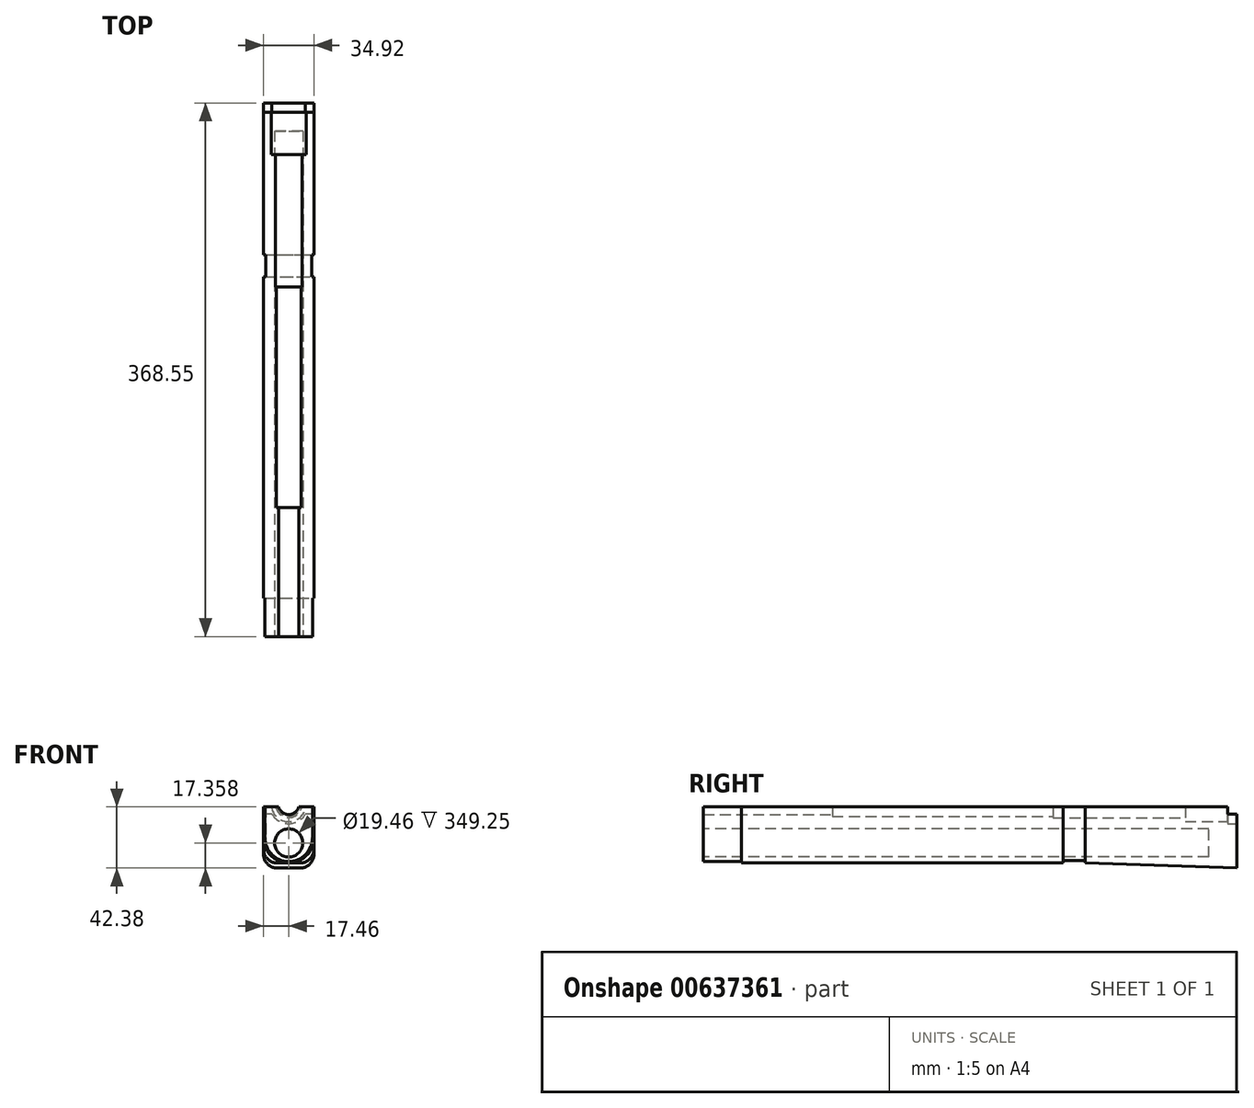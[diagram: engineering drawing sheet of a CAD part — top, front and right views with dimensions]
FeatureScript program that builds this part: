
annotation { "Feature Type Name" : "Feature", "Feature Type Description" : "" }
export const myFeature = defineFeature(function(context is Context, id is Id, definition is map)
    precondition{}
    {
        {
            var Q0;
            Q0=qCreatedBy(makeId("Front.planeOp"),FACE);
            var sketch = newSketch(context, id + "F0", { "sketchPlane" : qUnion([Q0])});
            skLineSegment(sketch, "E0", {"start": v(-17.45, -47.24) * mm, "end": v(17.45, -47.24) * mm});
            skLineSegment(sketch, "E1", {"start": v(-16.13, -1.78) * mm, "end": v(-16.13, -47.24) * mm});
            skLineSegment(sketch, "E2", {"start": v(16.13, -47.24) * mm, "end": v(16.13, -1.78) * mm});
            skLineSegment(sketch, "E3", {"start": v(-17.45, -1.78) * mm, "end": v(-17.45, -47.24) * mm});
            skLineSegment(sketch, "E4", {"start": v(17.45, -1.78) * mm, "end": v(12.57, -1.78) * mm});
            skLineSegment(sketch, "E5.trimOffspring", {"start": v(-12.57, -1.78) * mm, "end": v(-17.45, -1.78) * mm});
            skArc(sketch, "E6.converted", {"start": v(-12.57, -1.78) * mm, "mid": v(0, -12.7) * mm, "end": v(12.57, -1.78) * mm});
            skLineSegment(sketch, "E7", {"start": v(17.45, -6.83) * mm, "end": v(11.6, -6.83) * mm});
            skLineSegment(sketch, "E8", {"start": v(17.45, -1.78) * mm, "end": v(17.45, -47.24) * mm});
            skLineSegment(sketch, "E9.trimOffspring", {"start": v(-11.6, -6.83) * mm, "end": v(-17.45, -6.83) * mm});
            skArc(sketch, "E10.0", {"start": v(-13.34, -1.78) * mm, "mid": v(0, -13.46) * mm, "end": v(13.34, -1.78) * mm});
            skSolve(sketch);
        }
        {
            var Q0;
            {var subQ2=sQuery(id+"F0.wireOp",EDGE,"E2");Q0=makeQuery(id+"F0.imprint","IMPRINT",FACE,{"disambiguationData":[TD([[makeQuery(id+"F0.imprint","IMPRINT",EDGE,{"derivedFrom":subQ2}),-1.0]])]});}
            var Q1;
            {var subQ2=sQuery(id+"F0.wireOp",EDGE,"E1");Q1=makeQuery(id+"F0.imprint","IMPRINT",FACE,{"disambiguationData":[TD([[makeQuery(id+"F0.imprint","IMPRINT",EDGE,{"derivedFrom":subQ2}),-1.0]])]});}
            var Q2;
            {var subQ4=sQuery(id+"F0.wireOp",EDGE,"E1");Q2=makeQuery(id+"F0.imprint","IMPRINT",FACE,{"disambiguationData":[TD([[makeQuery(id+"F0.imprint","IMPRINT",EDGE,{"derivedFrom":subQ4}),1.0]])]});}
            var Q3;
            {var subQ0=sQuery(id+"F0.wireOp",EDGE,"E4");var subQ1=sQuery(id+"F0.wireOp",EDGE,"E2");var subQ2=makeQuery(id+"F0.imprint","INTERSECT",VERTEX,{"derivedFrom":[subQ1,subQ0]});Q3=makeQuery(id+"F0.imprint","IMPRINT",FACE,{"disambiguationData":[TD([[makeQuery(id+"F0.imprint","IMPRINT",EDGE,{"disambiguationData":[TD([[subQ2,1.0]])],"derivedFrom":subQ1}),1.0]])]});}
            var Q4;
            {var subQ0=sQuery(id+"F0.wireOp",EDGE,"E4");var subQ1=sQuery(id+"F0.wireOp",EDGE,"E2");var subQ2=makeQuery(id+"F0.imprint","INTERSECT",VERTEX,{"derivedFrom":[subQ1,subQ0]});Q4=makeQuery(id+"F0.imprint","IMPRINT",FACE,{"disambiguationData":[TD([[makeQuery(id+"F0.imprint","IMPRINT",EDGE,{"disambiguationData":[TD([[subQ2,1.0]])],"derivedFrom":subQ1}),-1.0]])]});}
            var Q5;
            {var subQ0=sQuery(id+"F0.wireOp",EDGE,"E5.trimOffspring");var subQ1=sQuery(id+"F0.wireOp",EDGE,"E1");var subQ2=makeQuery(id+"F0.imprint","INTERSECT",VERTEX,{"derivedFrom":[subQ1,subQ0]});Q5=makeQuery(id+"F0.imprint","IMPRINT",FACE,{"disambiguationData":[TD([[makeQuery(id+"F0.imprint","IMPRINT",EDGE,{"disambiguationData":[TD([[subQ2,-1.0]])],"derivedFrom":subQ1}),-1.0]])]});}
            var Q6;
            {var subQ5=sQuery(id+"F0.wireOp",EDGE,"E0");var subQ7=sQuery(id+"F0.wireOp",EDGE,"E1");var subQ8=makeQuery(id+"F0.imprint","INTERSECT",VERTEX,{"derivedFrom":[subQ5,subQ7]});Q6=makeQuery(id+"F0.imprint","IMPRINT",FACE,{"disambiguationData":[TD([[makeQuery(id+"F0.imprint","IMPRINT",EDGE,{"disambiguationData":[TD([[subQ8,-1.0]])],"derivedFrom":subQ5}),1.0]])]});}
            extrude(context, id + "F1", {"entities" : qUnion([Q0, Q1, Q2, Q3, Q4, Q5, Q6]), "depth" : 6.35 * mm, "offsetDistance" : 25.4 * mm});
        }
        {
            var Q0;
            Q0=makeQuery(id+"F1.opExtrude","CAP_FACE",FACE,{"disambiguationData":[OSD([sQuery(id+"F0.wireOp",EDGE,"E0"),sQuery(id+"F0.wireOp",EDGE,"8edb2757-4879-4a96-b7e5-693a79a6b6a4"),sQuery(id+"F0.wireOp",EDGE,"b94c221b-9bd1-4d43-af97-e907ac8222b8"),sQuery(id+"F0.wireOp",EDGE,"b538d115-4aab-44f9-98d3-6b26c575ee44"),sQuery(id+"F0.wireOp",EDGE,"78d40427-cc9b-45da-965b-9590cd821f86"),sQuery(id+"F0.wireOp",EDGE,"c01ce0f5-0f3a-4153-bfe7-1fc23657275d")])],"isStart":false});
            var sketch = newSketch(context, id + "F2", { "sketchPlane" : qUnion([Q0])});
            skLineSegment(sketch, "E11", {"start": v(-17.45, -47.24) * mm, "end": v(-17.45, -47.24) * mm});
            skArc(sketch, "E12", {"start": v(-11.93, -1.78) * mm, "mid": v(0, -12.07) * mm, "end": v(11.93, -1.78) * mm});
            skLineSegment(sketch, "E13", {"start": v(-16.13, -1.78) * mm, "end": v(-16.13, -47.24) * mm});
            skLineSegment(sketch, "E14", {"start": v(16.13, -1.78) * mm, "end": v(16.13, -47.24) * mm});
            skLineSegment(sketch, "E15", {"start": v(11.93, -1.78) * mm, "end": v(17.45, -1.78) * mm});
            skLineSegment(sketch, "E16", {"start": v(-11.93, -1.78) * mm, "end": v(-17.45, -1.78) * mm});
            skLineSegment(sketch, "E17", {"start": v(-17.45, -1.78) * mm, "end": v(-17.45, -47.24) * mm});
            skSolve(sketch);
        }
        {
            var Q0;
            {var subQ2=sQuery(id+"F2.wireOp",EDGE,"E13");Q0=makeQuery(id+"F2.imprint","IMPRINT",FACE,{"disambiguationData":[TD([[makeQuery(id+"F2.imprint","IMPRINT",EDGE,{"derivedFrom":subQ2}),1.0]])]});}
            var Q1;
            {var subQ0=sQuery(id+"F2.wireOp",EDGE,"E12");Q1=makeQuery(id+"F2.imprint","IMPRINT",FACE,{"disambiguationData":[TD([[makeQuery(id+"F2.imprint","IMPRINT",EDGE,{"derivedFrom":subQ0}),-1.0]])]});}
            var Q2;
            {var subQ0=sQuery(id+"F2.wireOp",EDGE,"E13");Q2=makeQuery(id+"F2.imprint","IMPRINT",FACE,{"disambiguationData":[TD([[makeQuery(id+"F2.imprint","IMPRINT",EDGE,{"derivedFrom":subQ0}),-1.0]])]});}
            var Q3;
            {var subQ0=sQuery(id+"F2.wireOp",EDGE,"E14");Q3=makeQuery(id+"F2.imprint","IMPRINT",FACE,{"disambiguationData":[TD([[makeQuery(id+"F2.imprint","IMPRINT",EDGE,{"derivedFrom":subQ0}),1.0]])]});}
            extrude(context, id + "F3", {"entities" : qUnion([Q0, Q1, Q2, Q3]), "operationType" : NewBodyOperationType.ADD, "depth" : 29.2 * mm, "offsetDistance" : 25.4 * mm});
        }
        {
            var Q0;
            Q0=makeQuery(id+"F3.opExtrude","CAP_FACE",FACE,{"disambiguationData":[OSD([sQuery(id+"F2.wireOp",EDGE,"E12"),sQuery(id+"F2.wireOp",EDGE,"E13"),sQuery(id+"F2.wireOp",EDGE,"E14"),sQuery(id+"F2.wireOp",EDGE,"f77e2a34-3a45-4c61-b7b2-087de49498f3"),sQuery(id+"F2.wireOp",EDGE,"be3fd59c-918e-4d32-9c2f-12a798890d1d"),sQuery(id+"F2.wireOp",EDGE,"E11")])],"isStart":false});
            var sketch = newSketch(context, id + "F4", { "sketchPlane" : qUnion([Q0])});
            skArc(sketch, "E18", {"start": v(-9.12, -1.78) * mm, "mid": v(0, -9.3) * mm, "end": v(9.12, -1.78) * mm});
            skLineSegment(sketch, "E19", {"start": v(-16.13, -1.78) * mm, "end": v(-16.13, -47.24) * mm});
            skLineSegment(sketch, "E20", {"start": v(16.13, -1.78) * mm, "end": v(16.13, -47.24) * mm});
            skLineSegment(sketch, "E21", {"start": v(17.45, -1.78) * mm, "end": v(9.12, -1.78) * mm});
            skLineSegment(sketch, "E22", {"start": v(-17.45, -1.78) * mm, "end": v(-9.12, -1.78) * mm});
            skLineSegment(sketch, "E23", {"start": v(-17.45, -47.24) * mm, "end": v(17.45, -47.24) * mm});
            skLineSegment(sketch, "E24", {"start": v(17.45, -47.24) * mm, "end": v(17.45, -1.78) * mm});
            skLineSegment(sketch, "E25", {"start": v(-17.45, -1.78) * mm, "end": v(-17.45, -47.24) * mm});
            skSolve(sketch);
        }
        {
            var Q0;
            Q0=qSketchRegion(id+"F4",true);
            extrude(context, id + "F5", {"entities" : qUnion([Q0]), "operationType" : NewBodyOperationType.ADD, "depth" : 69.06 * mm, "offsetDistance" : 25.4 * mm});
        }
        {
            var Q0;
            Q0=makeQuery(id+"F5.opExtrude","CAP_EDGE",EDGE,{"disambiguationData":[OSD([sQuery(id+"F4.wireOp",EDGE,"E23")])],"isStart":false});
            chamfer(context, id + "F6", {"entities" : qUnion([Q0]), "chamferType" : ChamferType.TWO_OFFSETS, "width1" : 6.6 * mm, "oppositeDirection" : false, "width2" : 196.06 * mm, "tangentPropagation" : true});
        }
        {
            var Q0;
            Q0=makeQuery(id+"F6.opChamfer","BLEND_EDGE",EDGE,{"blendedFrom":[makeQuery(id+"F5.opExtrude","CAP_EDGE",EDGE,{"disambiguationData":[OSD([sQuery(id+"F4.wireOp",EDGE,"E23")])],"isStart":false}),makeQuery(id+"F5.boolean.opBoolean","MERGE",FACE,{"derivedFrom":[makeQuery(id+"F3.boolean.opBoolean","MERGE",FACE,{"derivedFrom":[makeQuery(id+"F1.opExtrude","SWEPT_FACE",FACE,{"disambiguationData":[OSD([sQuery(id+"F0.wireOp",EDGE,"E3")])]}),makeQuery(id+"F3.opExtrude","SWEPT_FACE",FACE,{"disambiguationData":[OSD([sQuery(id+"F2.wireOp",EDGE,"E17")])]})]}),makeQuery(id+"F5.opExtrude","SWEPT_FACE",FACE,{"disambiguationData":[OSD([sQuery(id+"F4.wireOp",EDGE,"E25")])]})]})],"blendedInto":[makeQuery(id+"F5.boolean.opBoolean","MERGE",FACE,{"derivedFrom":[makeQuery(id+"F3.boolean.opBoolean","MERGE",FACE,{"derivedFrom":[makeQuery(id+"F1.opExtrude","SWEPT_FACE",FACE,{"disambiguationData":[OSD([sQuery(id+"F0.wireOp",EDGE,"E3")])]}),makeQuery(id+"F3.opExtrude","SWEPT_FACE",FACE,{"disambiguationData":[OSD([sQuery(id+"F2.wireOp",EDGE,"E17")])]})]}),makeQuery(id+"F5.opExtrude","SWEPT_FACE",FACE,{"disambiguationData":[OSD([sQuery(id+"F4.wireOp",EDGE,"E25")])]})]})]});
            var Q1;
            Q1=makeQuery(id+"F6.opChamfer","BLEND_EDGE",EDGE,{"blendedFrom":[makeQuery(id+"F5.opExtrude","CAP_EDGE",EDGE,{"disambiguationData":[OSD([sQuery(id+"F4.wireOp",EDGE,"E23")])],"isStart":false}),makeQuery(id+"F5.boolean.opBoolean","MERGE",FACE,{"derivedFrom":[makeQuery(id+"F3.boolean.opBoolean","MERGE",FACE,{"derivedFrom":[makeQuery(id+"F1.opExtrude","SWEPT_FACE",FACE,{"disambiguationData":[OSD([sQuery(id+"F0.wireOp",EDGE,"2a34f45b-83aa-449b-ac8a-cdb24f63008b")])]}),makeQuery(id+"F3.opExtrude","SWEPT_FACE",FACE,{"disambiguationData":[OSD([sQuery(id+"F2.wireOp",EDGE,"fa13c2eb-5be7-4b32-a947-3f863f632ee6")])]})]}),makeQuery(id+"F5.opExtrude","SWEPT_FACE",FACE,{"disambiguationData":[OSD([sQuery(id+"F4.wireOp",EDGE,"E24")])]})]})],"blendedInto":[makeQuery(id+"F5.boolean.opBoolean","MERGE",FACE,{"derivedFrom":[makeQuery(id+"F3.boolean.opBoolean","MERGE",FACE,{"derivedFrom":[makeQuery(id+"F1.opExtrude","SWEPT_FACE",FACE,{"disambiguationData":[OSD([sQuery(id+"F0.wireOp",EDGE,"2a34f45b-83aa-449b-ac8a-cdb24f63008b")])]}),makeQuery(id+"F3.opExtrude","SWEPT_FACE",FACE,{"disambiguationData":[OSD([sQuery(id+"F2.wireOp",EDGE,"fa13c2eb-5be7-4b32-a947-3f863f632ee6")])]})]}),makeQuery(id+"F5.opExtrude","SWEPT_FACE",FACE,{"disambiguationData":[OSD([sQuery(id+"F4.wireOp",EDGE,"E24")])]})]})]});
            fillet(context, id + "F7", {"entities" : qUnion([Q0, Q1]), "radius" : 9.65 * mm, "tangentPropagation" : true, "allowEdgeOverflow" : false});
        }
        {
            var Q0;
            Q0=makeQuery(id+"F5.opExtrude","CAP_FACE",FACE,{"disambiguationData":[OSD([sQuery(id+"F4.wireOp",EDGE,"E18"),sQuery(id+"F4.wireOp",EDGE,"E21"),sQuery(id+"F4.wireOp",EDGE,"E22"),sQuery(id+"F4.wireOp",EDGE,"E23"),sQuery(id+"F4.wireOp",EDGE,"E24"),sQuery(id+"F4.wireOp",EDGE,"E25")])],"isStart":false});
            var sketch = newSketch(context, id + "F8", { "sketchPlane" : qUnion([Q0])});
            skLineSegment(sketch, "E26.0", {"start": v(-15.92, -1.78) * mm, "end": v(-15.93, -23.19) * mm});
            skLineSegment(sketch, "E27.0", {"start": v(15.92, -1.78) * mm, "end": v(15.93, -23.19) * mm});
            skArc(sketch, "E28", {"start": v(-15.93, -23.19) * mm, "mid": v(0, -39.12) * mm, "end": v(15.93, -23.19) * mm});
            skLineSegment(sketch, "E29", {"start": v(-15.92, -1.78) * mm, "end": v(-9.12, -1.78) * mm});
            skLineSegment(sketch, "E30", {"start": v(15.92, -1.78) * mm, "end": v(9.12, -1.78) * mm});
            skArc(sketch, "E31", {"start": v(-9.12, -1.78) * mm, "mid": v(0, -9.3) * mm, "end": v(9.12, -1.78) * mm});
            skSolve(sketch);
        }
        {
            var Q0;
            Q0=makeQuery(id+"F8.imprint","IMPRINT",FACE,{"disambiguationData":[TD([[makeQuery(id+"F8.imprint","IMPRINT",EDGE,{"derivedFrom":sQuery(id+"F8.wireOp",EDGE,"E26.0")}),1.0]])]});
            extrude(context, id + "F9", {"entities" : qUnion([Q0]), "operationType" : NewBodyOperationType.ADD, "depth" : 15.42 * mm, "offsetDistance" : 25.4 * mm});
        }
        {
            var Q0;
            Q0=makeQuery(id+"F9.opExtrude","CAP_FACE",FACE,{"disambiguationData":[OSD([sQuery(id+"F8.wireOp",EDGE,"E26.0"),sQuery(id+"F8.wireOp",EDGE,"E27.0"),sQuery(id+"F8.wireOp",EDGE,"E28"),sQuery(id+"F8.wireOp",EDGE,"E29"),sQuery(id+"F8.wireOp",EDGE,"E30"),sQuery(id+"F8.wireOp",EDGE,"E31")])],"isStart":false});
            var sketch = newSketch(context, id + "F10", { "sketchPlane" : qUnion([Q0])});
            skLineSegment(sketch, "E32", {"start": v(9.12, -1.78) * mm, "end": v(17.46, -1.78) * mm});
            skArc(sketch, "E33", {"start": v(-9.12, -1.78) * mm, "mid": v(0, -9.3) * mm, "end": v(9.12, -1.78) * mm});
            skLineSegment(sketch, "E34.MirrorCS", {"start": v(-9.12, -1.78) * mm, "end": v(-17.46, -1.78) * mm});
            skLineSegment(sketch, "E35.MirrorCS", {"start": v(17.46, -1.78) * mm, "end": v(17.46, -23.18) * mm});
            skLineSegment(sketch, "E36.MirrorCS", {"start": v(-17.46, -1.78) * mm, "end": v(-17.46, -23.18) * mm});
            skArc(sketch, "E37", {"start": v(-17.46, -23.18) * mm, "mid": v(0, -40.64) * mm, "end": v(17.46, -23.18) * mm});
            skSolve(sketch);
        }
        {
            var Q0;
            {var subQ0=sQuery(id+"F10.wireOp",EDGE,"E35.MirrorCS");Q0=makeQuery(id+"F10.imprint","IMPRINT",FACE,{"disambiguationData":[TD([[makeQuery(id+"F10.imprint","IMPRINT",EDGE,{"derivedFrom":subQ0}),-1.0]])]});}
            var Q1;
            {var subQ2=sQuery(id+"F10.wireOp",EDGE,"E33");Q1=makeQuery(id+"F10.imprint","IMPRINT",FACE,{"disambiguationData":[TD([[makeQuery(id+"F10.imprint","IMPRINT",EDGE,{"derivedFrom":subQ2}),-1.0]])]});}
            extrude(context, id + "F11", {"entities" : qUnion([Q0, Q1]), "operationType" : NewBodyOperationType.ADD, "depth" : 6.96 * mm, "offsetDistance" : 25.4 * mm});
        }
        {
            var Q0;
            Q0=makeQuery(id+"F11.opExtrude","CAP_FACE",FACE,{"disambiguationData":[OSD([sQuery(id+"F10.wireOp",EDGE,"E32"),sQuery(id+"F10.wireOp",EDGE,"E33"),sQuery(id+"F10.wireOp",EDGE,"E34.MirrorCS"),sQuery(id+"F10.wireOp",EDGE,"E35.MirrorCS"),sQuery(id+"F10.wireOp",EDGE,"E36.MirrorCS"),sQuery(id+"F10.wireOp",EDGE,"E37")])],"isStart":false});
            var sketch = newSketch(context, id + "F12", { "sketchPlane" : qUnion([Q0])});
            skLineSegment(sketch, "E38", {"start": v(17.46, -1.78) * mm, "end": v(8.45, -1.78) * mm});
            skLineSegment(sketch, "E39", {"start": v(-17.46, -1.78) * mm, "end": v(-17.46, -23.18) * mm});
            skLineSegment(sketch, "E40", {"start": v(17.46, -1.78) * mm, "end": v(17.46, -23.18) * mm});
            skArc(sketch, "E41", {"start": v(-17.46, -23.18) * mm, "mid": v(0, -40.64) * mm, "end": v(17.46, -23.18) * mm});
            skLineSegment(sketch, "E42", {"start": v(-17.46, -1.78) * mm, "end": v(-8.45, -1.78) * mm});
            skArc(sketch, "E43", {"start": v(-8.45, -1.78) * mm, "mid": v(0, -8.64) * mm, "end": v(8.45, -1.78) * mm});
            skSolve(sketch);
        }
        {
            var Q0;
            {var subQ0=sQuery(id+"F12.wireOp",EDGE,"E39");Q0=makeQuery(id+"F12.imprint","IMPRINT",FACE,{"disambiguationData":[TD([[makeQuery(id+"F12.imprint","IMPRINT",EDGE,{"derivedFrom":subQ0}),1.0]])]});}
            var Q1;
            {var subQ2=sQuery(id+"F12.wireOp",EDGE,"E43");Q1=makeQuery(id+"F12.imprint","IMPRINT",FACE,{"disambiguationData":[TD([[makeQuery(id+"F12.imprint","IMPRINT",EDGE,{"derivedFrom":subQ2}),-1.0]])]});}
            extrude(context, id + "F13", {"entities" : qUnion([Q0, Q1]), "operationType" : NewBodyOperationType.ADD, "depth" : 152.4 * mm, "offsetDistance" : 25.4 * mm});
        }
        {
            var Q0;
            Q0=makeQuery(id+"F13.opExtrude","CAP_FACE",FACE,{"disambiguationData":[OSD([sQuery(id+"F12.wireOp",EDGE,"a289bdf0-b78a-4701-b150-00bdd420398b"),sQuery(id+"F12.wireOp",EDGE,"E38"),sQuery(id+"F12.wireOp",EDGE,"E39"),sQuery(id+"F12.wireOp",EDGE,"E40"),sQuery(id+"F12.wireOp",EDGE,"E41"),sQuery(id+"F12.wireOp",EDGE,"E42")])],"isStart":false});
            var sketch = newSketch(context, id + "F14", { "sketchPlane" : qUnion([Q0])});
            skArc(sketch, "E44", {"start": v(-7.02, -1.78) * mm, "mid": v(0, -7.24) * mm, "end": v(7.02, -1.78) * mm});
            skLineSegment(sketch, "E45", {"start": v(17.46, -1.78) * mm, "end": v(7.02, -1.78) * mm});
            skLineSegment(sketch, "E46", {"start": v(-17.46, -1.78) * mm, "end": v(-17.46, -23.18) * mm});
            skLineSegment(sketch, "E47", {"start": v(17.46, -1.78) * mm, "end": v(17.46, -23.18) * mm});
            skArc(sketch, "E48", {"start": v(-17.46, -23.18) * mm, "mid": v(0, -40.64) * mm, "end": v(17.46, -23.18) * mm});
            skLineSegment(sketch, "E49", {"start": v(-17.46, -1.78) * mm, "end": v(-7.02, -1.78) * mm});
            skSolve(sketch);
        }
        {
            var Q0;
            {var subQ1=sQuery(id+"F14.wireOp",EDGE,"E46");Q0=makeQuery(id+"F14.imprint","IMPRINT",FACE,{"disambiguationData":[TD([[makeQuery(id+"F14.imprint","IMPRINT",EDGE,{"derivedFrom":subQ1}),1.0]])]});}
            var Q1;
            {var subQ0=sQuery(id+"F14.wireOp",EDGE,"E44");Q1=makeQuery(id+"F14.imprint","IMPRINT",FACE,{"disambiguationData":[TD([[makeQuery(id+"F14.imprint","IMPRINT",EDGE,{"derivedFrom":subQ0}),-1.0]])]});}
            extrude(context, id + "F15", {"entities" : qUnion([Q0, Q1]), "operationType" : NewBodyOperationType.ADD, "depth" : 89.15 * mm, "offsetDistance" : 25.4 * mm});
        }
        {
            var Q0;
            Q0=makeQuery(id+"F15.opExtrude","CAP_FACE",FACE,{"disambiguationData":[OSD([sQuery(id+"F14.wireOp",EDGE,"E44"),sQuery(id+"F14.wireOp",EDGE,"E45"),sQuery(id+"F14.wireOp",EDGE,"E46"),sQuery(id+"F14.wireOp",EDGE,"E47"),sQuery(id+"F14.wireOp",EDGE,"E48"),sQuery(id+"F14.wireOp",EDGE,"E49")])],"isStart":false});
            var sketch = newSketch(context, id + "F16", { "sketchPlane" : qUnion([Q0])});
            skLineSegment(sketch, "E50", {"start": v(17.46, -1.78) * mm, "end": v(16.44, -1.78) * mm});
            skLineSegment(sketch, "E51", {"start": v(-16.44, -1.78) * mm, "end": v(-17.46, -1.78) * mm});
            skLineSegment(sketch, "E52", {"start": v(-17.46, -1.78) * mm, "end": v(-17.46, -23.17) * mm});
            skLineSegment(sketch, "E53", {"start": v(17.46, -1.78) * mm, "end": v(17.46, -23.18) * mm});
            skArc(sketch, "E54", {"start": v(-17.46, -23.17) * mm, "mid": v(0, -40.64) * mm, "end": v(17.46, -23.17) * mm});
            skLineSegment(sketch, "E55.0", {"start": v(-16.44, -1.78) * mm, "end": v(-16.45, -23.18) * mm});
            skLineSegment(sketch, "E56.0", {"start": v(16.44, -1.78) * mm, "end": v(16.45, -23.18) * mm});
            skArc(sketch, "E57.0", {"start": v(-16.45, -23.18) * mm, "mid": v(0, -39.62) * mm, "end": v(16.45, -23.18) * mm});
            skCircle(sketch, "E58", {"center": v(0, -26.8) * mm, "radius": 9.73 * mm});
            skSolve(sketch);
        }
        {
            var Q0;
            Q0=makeQuery(id+"F16.imprint","IMPRINT",FACE,{"disambiguationData":[TD([[makeQuery(id+"F16.imprint","IMPRINT",EDGE,{"derivedFrom":sQuery(id+"F16.wireOp",EDGE,"E50")}),1.0]])]});
            extrude(context, id + "F17", {"entities" : qUnion([Q0]), "operationType" : NewBodyOperationType.REMOVE, "oppositeDirection" : true, "depth" : 26.5 * mm, "offsetDistance" : 25.4 * mm});
        }
        {
            var Q0;
            Q0=makeQuery(id+"F16.imprint","IMPRINT",FACE,{"disambiguationData":[TD([[makeQuery(id+"F16.imprint","IMPRINT",EDGE,{"derivedFrom":sQuery(id+"F16.wireOp",EDGE,"E58")}),1.0]])]});
            extrude(context, id + "F18", {"entities" : qUnion([Q0]), "operationType" : NewBodyOperationType.REMOVE, "oppositeDirection" : true, "depth" : 349.25 * mm, "offsetDistance" : 25.4 * mm});
        }
        {
            var Q0;
            {var subQ0=sQuery(id+"F0.wireOp",EDGE,"E4");var subQ1=sQuery(id+"F0.wireOp",EDGE,"E2");var subQ2=makeQuery(id+"F0.imprint","INTERSECT",VERTEX,{"derivedFrom":[subQ1,subQ0]});Q0=makeQuery(id+"F0.imprint","IMPRINT",FACE,{"disambiguationData":[TD([[makeQuery(id+"F0.imprint","IMPRINT",EDGE,{"disambiguationData":[TD([[subQ2,1.0]])],"derivedFrom":subQ1}),-1.0]])]});}
            var Q1;
            {var subQ0=sQuery(id+"F0.wireOp",EDGE,"E4");var subQ1=sQuery(id+"F0.wireOp",EDGE,"E2");var subQ2=makeQuery(id+"F0.imprint","INTERSECT",VERTEX,{"derivedFrom":[subQ1,subQ0]});Q1=makeQuery(id+"F0.imprint","IMPRINT",FACE,{"disambiguationData":[TD([[makeQuery(id+"F0.imprint","IMPRINT",EDGE,{"disambiguationData":[TD([[subQ2,1.0]])],"derivedFrom":subQ1}),1.0]])]});}
            var Q2;
            {var subQ0=sQuery(id+"F0.wireOp",EDGE,"E5.trimOffspring");var subQ1=sQuery(id+"F0.wireOp",EDGE,"E1");var subQ2=makeQuery(id+"F0.imprint","INTERSECT",VERTEX,{"derivedFrom":[subQ1,subQ0]});Q2=makeQuery(id+"F0.imprint","IMPRINT",FACE,{"disambiguationData":[TD([[makeQuery(id+"F0.imprint","IMPRINT",EDGE,{"disambiguationData":[TD([[subQ2,-1.0]])],"derivedFrom":subQ1}),1.0]])]});}
            var Q3;
            {var subQ0=sQuery(id+"F0.wireOp",EDGE,"E5.trimOffspring");var subQ1=sQuery(id+"F0.wireOp",EDGE,"E1");var subQ2=makeQuery(id+"F0.imprint","INTERSECT",VERTEX,{"derivedFrom":[subQ1,subQ0]});Q3=makeQuery(id+"F0.imprint","IMPRINT",FACE,{"disambiguationData":[TD([[makeQuery(id+"F0.imprint","IMPRINT",EDGE,{"disambiguationData":[TD([[subQ2,-1.0]])],"derivedFrom":subQ1}),-1.0]])]});}
            extrude(context, id + "F19", {"entities" : qUnion([Q0, Q1, Q2, Q3]), "operationType" : NewBodyOperationType.REMOVE, "depth" : 6.35 * mm, "offsetDistance" : 25.4 * mm});
        }
    });
